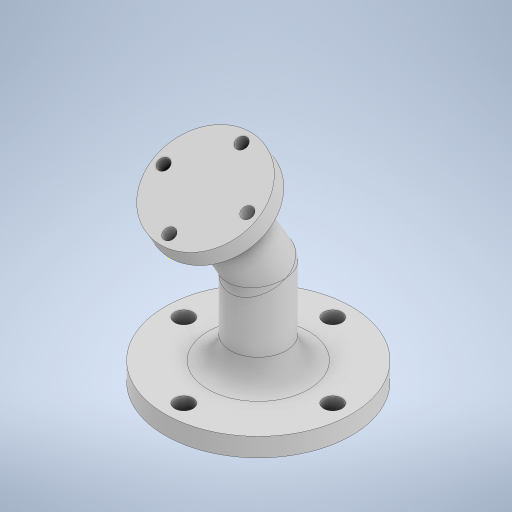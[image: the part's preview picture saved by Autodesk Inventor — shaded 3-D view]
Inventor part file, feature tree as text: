
AUTODESK INVENTOR PART (.ipt)
format: ipt  version: 2023 (Build 270158000, 158)  size: 352,256 bytes
history: native  units: in
note: dims shown in document units (in); Inventor stores cm internally (conversion verified against a paired STEP export)
features: sketch x10, extrude x6, other x5, fillet x3, plane x2, projected_geometry x1
ambient origin geometry x8: Origin, YZ Plane, XZ Plane, XY Plane, X Axis, Y Axis, Z Axis, Center Point
bodies: Body1 (feature_tree)
feature tree (27):
  other  "Sólido1"
  extrude  "Extrusión1"  Depth=0.1969in TaperAngle=0.0deg
  extrude  "Extrusión2"  Depth=1.5748in TaperAngle=360.0deg
  extrude  "Extrusión3"  Depth=0.1969in
  sketch  "Boceto4"  dims[d12=0.9843in d13=0.0in d17=0.5906in d18=0.9843in d19=0.0in d20=0.2362in]
  sketch  "Boceto5"  dims[d21=0.2362in d22=1.1024in d23=0.1969in d24=0.0in]
  plane  "Plano de trabajo1"
  sketch  "Boceto6"  dims[d25=0.0394in d26=0.122in]
  plane  "Plano de trabajo2"
  extrude  "Extrusión5"  Depth=0.2362in
  other  "Suprimir cara1"
  other  "Suprimir cara2"
  other  "Suprimir cara3"
  other  "Suprimir cara4"
  fillet  "Empalme2"  Radius=0.9843in
  fillet  "Empalme3"  Radius=0.2362in
  sketch  "Boceto8"  dims[d31=0.1969in d32=0.0in]
  sketch  "Boceto9"  dims[d14=0.0in]
  extrude  "Extrusión6"  Depth=0.1969in
  fillet  "Empalme4"  Radius=0.1969in
  extrude  "Extrusión7"  Depth=0.0394in
  sketch  "Boceto1"  dims[d0=1.9685in d1=0.1969in d2=0.0in]
  sketch  "Boceto2"  dims[d4=0.1937in d5=1.5748in d7=360.0deg]
  sketch  "Boceto3"  dims[d9=0.1969in d10=0.0in d11=0.5906in]
  sketch  "Boceto7"  dims[d27=1.5748in d29=360.0deg]
  projected_geometry  "Contorno proyectado1"
  sketch  "Boceto10"  dims[d15=0.0in d16=0.0in d28=0.0in]
